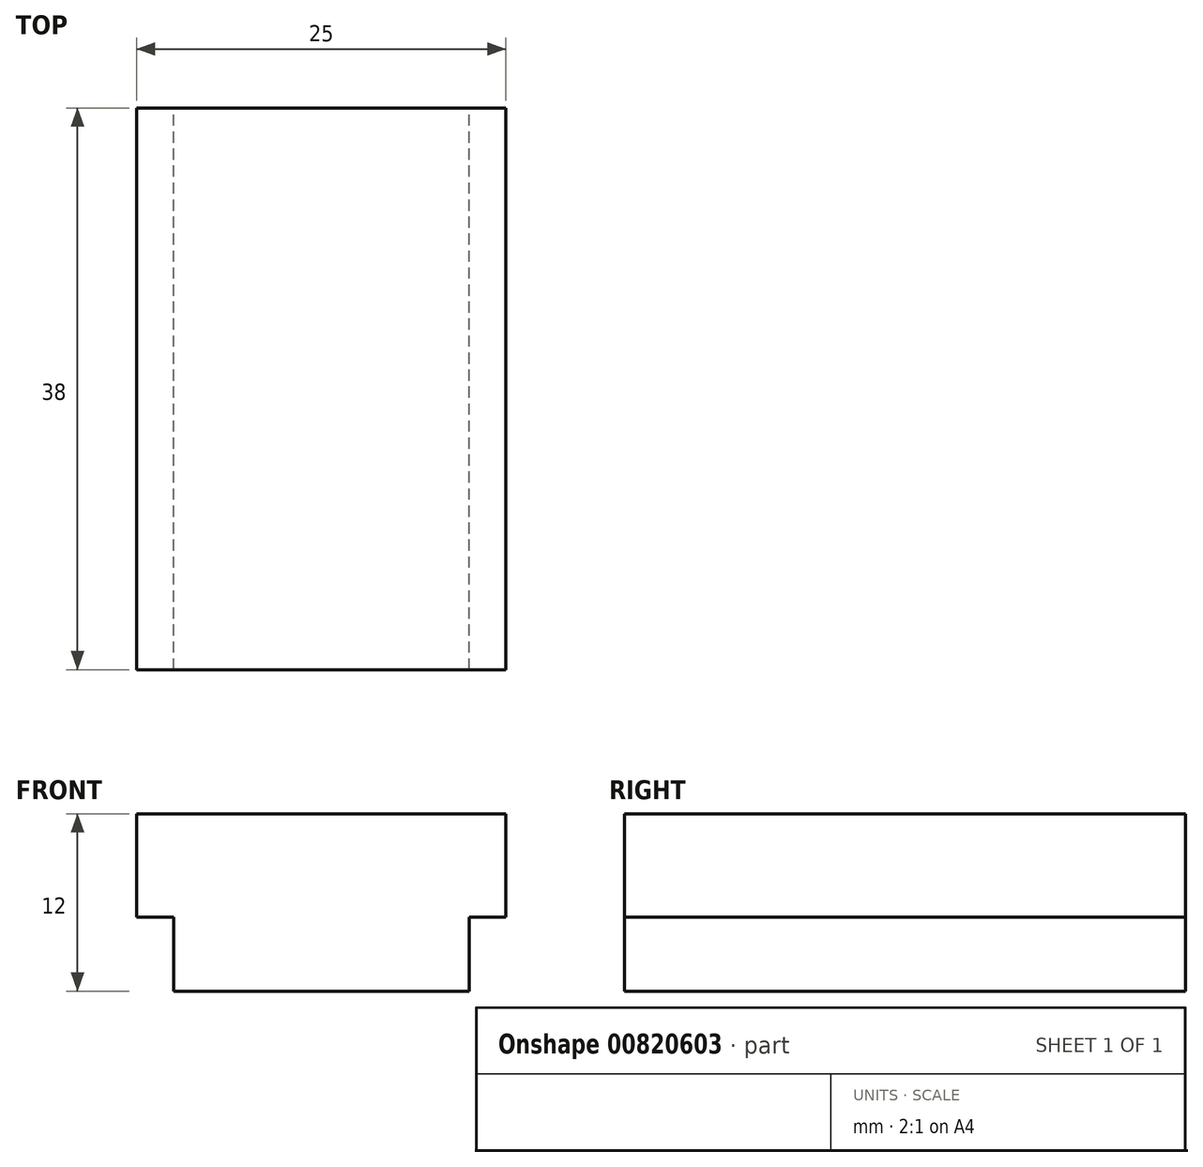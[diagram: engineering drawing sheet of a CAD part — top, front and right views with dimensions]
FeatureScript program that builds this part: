
annotation { "Feature Type Name" : "Feature", "Feature Type Description" : "" }
export const myFeature = defineFeature(function(context is Context, id is Id, definition is map)
    precondition{}
    {
        {
            var Q0;
            Q0=qCreatedBy(makeId("Top.planeOp"),FACE);
            var sketch = newSketch(context, id + "F0", { "sketchPlane" : qUnion([Q0])});
            skLineSegment(sketch, "E0.bottom", {"start": v(-29.18, 21.1) * mm, "end": v(-4.18, 21.1) * mm});
            skLineSegment(sketch, "E0.top", {"start": v(-29.18, -16.9) * mm, "end": v(-4.18, -16.9) * mm});
            skLineSegment(sketch, "E0.left", {"start": v(-29.18, 21.1) * mm, "end": v(-29.18, -16.9) * mm});
            skLineSegment(sketch, "E0.right", {"start": v(-4.18, 21.1) * mm, "end": v(-4.18, -16.9) * mm});
            skSolve(sketch);
        }
        {
            var Q0;
            Q0=qSketchRegion(id+"F0",true);
            extrude(context, id + "F1", {"entities" : qUnion([Q0]), "depth" : 12 * mm, "offsetDistance" : 25 * mm});
        }
        {
            var Q0;
            Q0=makeQuery(id+"F1.opExtrude","CAP_FACE",FACE,{"disambiguationData":[OSD([sQuery(id+"F0.wireOp",EDGE,"E0.bottom"),sQuery(id+"F0.wireOp",EDGE,"E0.top"),sQuery(id+"F0.wireOp",EDGE,"E0.left"),sQuery(id+"F0.wireOp",EDGE,"E0.right")])],"isStart":true});
            var sketch = newSketch(context, id + "F2", { "sketchPlane" : qUnion([Q0])});
            skLineSegment(sketch, "E1.left", {"start": v(-26.68, 16.9) * mm, "end": v(-26.68, -21.1) * mm});
            skLineSegment(sketch, "E1.right", {"start": v(-6.68, 16.9) * mm, "end": v(-6.68, -21.1) * mm});
            skLineSegment(sketch, "E2.bottom", {"start": v(-29.18, 16.9) * mm, "end": v(-26.68, 16.9) * mm});
            skLineSegment(sketch, "E2.top", {"start": v(-29.18, -21.1) * mm, "end": v(-26.68, -21.1) * mm});
            skLineSegment(sketch, "E2.left", {"start": v(-29.18, 16.9) * mm, "end": v(-29.18, -21.1) * mm});
            skLineSegment(sketch, "E3.bottom", {"start": v(-4.18, 16.9) * mm, "end": v(-6.68, 16.9) * mm});
            skLineSegment(sketch, "E3.top", {"start": v(-4.18, -21.1) * mm, "end": v(-6.68, -21.1) * mm});
            skLineSegment(sketch, "E3.left", {"start": v(-4.18, 16.9) * mm, "end": v(-4.18, -21.1) * mm});
            skSolve(sketch);
        }
        {
            var Q0;
            Q0 = qSketchRegion(id + "F2", true);
            extrude(context, id + "F3", {"entities" : qUnion([Q0]), "operationType" : NewBodyOperationType.REMOVE, "oppositeDirection" : true, "depth" : 5 * mm, "offsetDistance" : 25 * mm});
        }
    });
